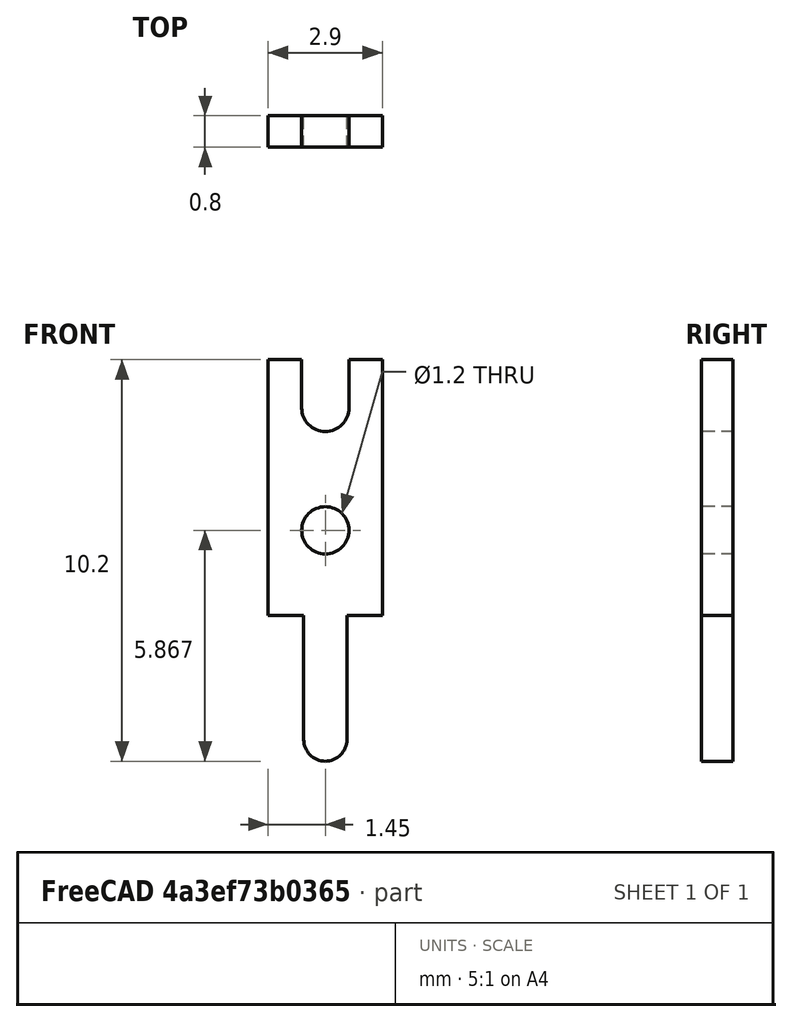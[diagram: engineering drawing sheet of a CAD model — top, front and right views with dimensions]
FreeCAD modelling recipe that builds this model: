
FCSTD DOCUMENT  (FreeCAD 0.17R12018 (Git))
Label: Pin_d1.2mm_L10.2mm_W2.9mm_FlatFork
License: All rights reserved
LicenseURL: http://en.wikipedia.org/wiki/All_rights_reserved
objects: Spreadsheet::Sheet×1, Sketcher::SketchObject×1, PartDesign::Pad×1, PartDesign::Body×1, App::Part×1
note: 4 computed .brp shape members not serialized (recipe doc carries the construction recipe); baked Part::Feature solids carry a one-line shape summary decoded from their .brp

FEATURE [Spreadsheet::Sheet] Spreadsheet  label="dimensions"
  cells = A1="L"; B1(L)=10.199999999999999; A2="Wtop"; B2(Wtop)=2.8999999999999999; A3="Wbottom"; B3(Wbottom)=1.1000000000000001; A4="Lbottom"; B4(Lbottom)=3.7000000000000002; A5="Wfork"; B5(Wfork)=1.2; A6="FractionFork"; B6(FractionFork)=0.25; A7="thick"; B7(thick)=0.80000000000000004
FEATURE [Sketcher::SketchObject] Sketch
  MapMode = 5
  Placement = pos=(0,0,0) rot=(0,0.707107,0.707107;3.14159rad)
  Support = -> [XZ_Plane001]
  expr: Constraints[44] = (dimensions.L - dimensions.Lbottom) * 0.66669999999999996
  expr: Constraints[43] = dimensions.Wfork / 2
  expr: Constraints[40] = dimensions.Wtop
  expr: Constraints[38] = dimensions.Wbottom
  expr: Constraints[39] = (dimensions.Wtop - dimensions.Wbottom) / 2
  expr: Constraints[37] = dimensions.Lbottom - dimensions.Wbottom / 2
  expr: Constraints[32] = dimensions.L - dimensions.Lbottom
  expr: Constraints[19] = dimensions.Wfork
  sketch-geometry (15):
    g0: LineSegment StartX=-1.45 StartY=6.5 StartZ=0 EndX=-1.45 EndY=0 EndZ=0
    g1: LineSegment StartX=-1.45 StartY=0 StartZ=0 EndX=-0.55 EndY=0 EndZ=0
    g2: LineSegment StartX=-0.55 StartY=0 StartZ=0 EndX=-0.55 EndY=-3.15 EndZ=0
    g3: LineSegment StartX=0.55 StartY=0 StartZ=0 EndX=0.55 EndY=-3.15 EndZ=0
    g4: LineSegment StartX=0.55 StartY=0 StartZ=0 EndX=1.45 EndY=0 EndZ=0
    g5: LineSegment StartX=1.45 StartY=0 StartZ=0 EndX=1.45 EndY=6.5 EndZ=0
    g6: LineSegment StartX=1.45 StartY=6.5 StartZ=0 EndX=0.6 EndY=6.5 EndZ=0
    g7: LineSegment StartX=0.6 StartY=6.5 StartZ=0 EndX=0.6 EndY=5.275 EndZ=0
    g8: LineSegment StartX=-0.6 StartY=5.275 StartZ=0 EndX=-0.6 EndY=6.5 EndZ=0
    g9: LineSegment StartX=-0.6 StartY=6.5 StartZ=0 EndX=-1.45 EndY=6.5 EndZ=0
    g10: ArcOfCircle CenterX=0 CenterY=-3.15 CenterZ=0 NormalX=0 NormalY=0 NormalZ=1 Radius=0.55 StartAngle=3.14159 EndAngle=6.28319
    g11: ArcOfCircle CenterX=0 CenterY=5.275 CenterZ=0 NormalX=0 NormalY=0 NormalZ=1 Radius=0.6 StartAngle=3.14159 EndAngle=6.28319
    g12: LineSegment [constr] StartX=-0.55 StartY=-3.15 StartZ=0 EndX=0.55 EndY=-3.15 EndZ=0
    g13: LineSegment [constr] StartX=-0.6 StartY=5.275 StartZ=0 EndX=0.6 EndY=5.275 EndZ=0
    g14: Circle CenterX=0 CenterY=2.16645 CenterZ=0 NormalX=0 NormalY=0 NormalZ=1 Radius=0.6
  constraints (45):
    c: PointOnObject(g3,g-1)
    c: Horizontal(g6)
    c: Vertical(g7)
    c: Vertical(g8)
    c: Coincident(g9,g0)
    c: Horizontal(g9)
    c: Equal(g9,g6)
    c: PointOnObject(g10,g-2)
    c: Coincident(g8,g9)
    c: Coincident(g6,g7)
    c: Coincident(g5,g6)
    c: Coincident(g11,g8)
    c: Coincident(g11,g7)
    c: Coincident(g12,g3)
    c: Coincident(g13,g8)
    c: Coincident(g13,g7)
    c: Horizontal(g13)
    c: PointOnObject(g11,g13)
    c: DistanceY(g8,g6) = 0
    c: DistanceX(g8,g6) = 1.2
    c: DistanceY(g8,g8) = 1.225
    c: Coincident(g12,g2)
    c: Coincident(g2,g10)
    c: Coincident(g3,g10)
    c: PointOnObject(g10,g12)
    c: Horizontal(g12)
    c: Vertical(g3)
    c: Vertical(g2)
    c: Horizontal(g1)
    c: Horizontal(g4)
    c: Vertical(g5)
    c: Vertical(g0)
    c: DistanceY(g5,g5) = 6.5
    c: Coincident(g5,g4)
    c: Coincident(g0,g1)
    c: Coincident(g4,g3)
    c: Coincident(g1,g2)
    c: DistanceY(g3,g3) = 3.15
    c: DistanceX(g2,g3) = 1.1
    c: DistanceX(g1,g1) = 0.9
    c: DistanceX(g0,g5) = 2.9
    c: PointOnObject(g1,g-1)
    c: PointOnObject(g14,g-2)
    c: Radius(g14) = 0.6
    c: DistanceY(g14,g8) = 4.33355
FEATURE [PartDesign::Pad] Pad  label="Pin_d1.2mm_L10.2mm_W2.9mm_FlatFork"
  Length = 0.8
  Length2 = 100
  Midplane = true
  Placement = pos=(0,0,0) rot=(1,0,0;1.5708rad)
  Profile = -> Sketch
  Type = 0
  expr: Length = dimensions.thick
FEATURE [PartDesign::Body] PadBody  label="Body"
  Group = -> [Sketch,Pad]
  Origin = -> Origin001
  Tip = -> Pad
FEATURE [App::Part] Part
  Group = -> [PadBody]
  License = CC BY 3.0
  LicenseURL = http://creativecommons.org/licenses/by/3.0/
  Origin = -> Origin
